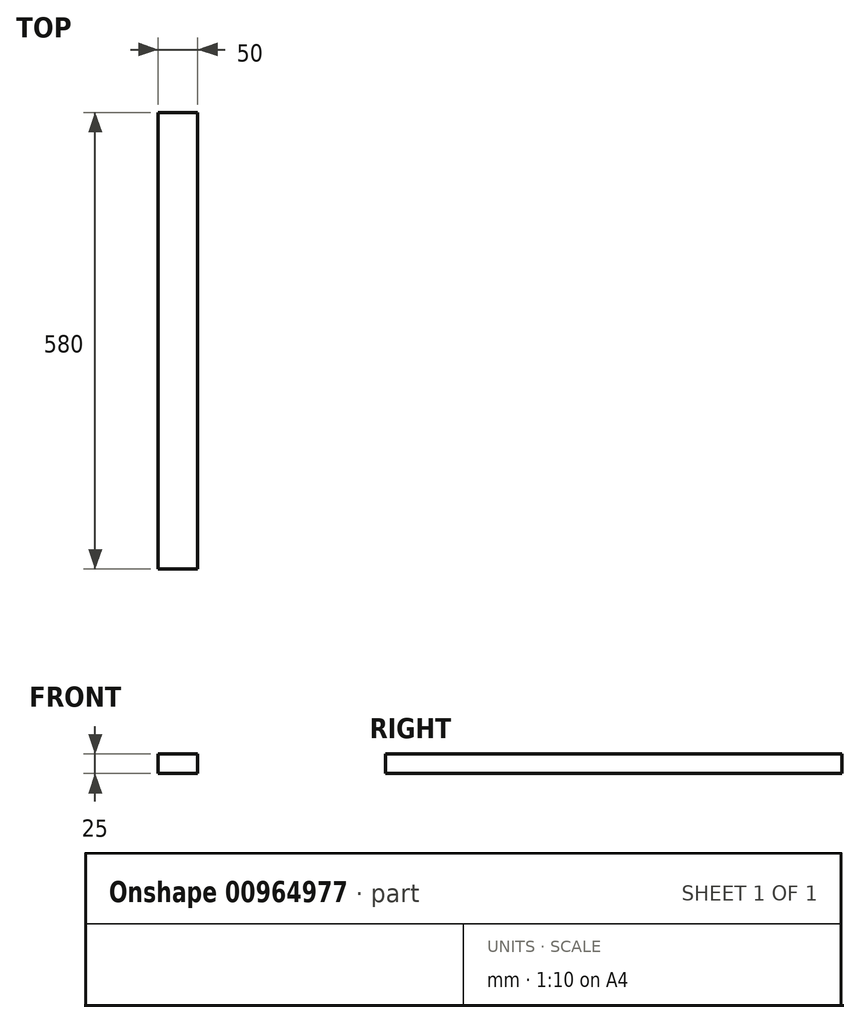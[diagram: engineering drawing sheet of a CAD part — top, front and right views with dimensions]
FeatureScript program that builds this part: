
annotation { "Feature Type Name" : "Feature", "Feature Type Description" : "" }
export const myFeature = defineFeature(function(context is Context, id is Id, definition is map)
    precondition{}
    {
        {
            var Q0;
            Q0=qCreatedBy(makeId("Top.planeOp"),FACE);
            var sketch = newSketch(context, id + "F0", { "sketchPlane" : qUnion([Q0])});
            skLineSegment(sketch, "E0.bottom", {"start": v(-2828.7, -249.1) * mm, "end": v(-2878.7, -249.1) * mm});
            skLineSegment(sketch, "E0.top", {"start": v(-2828.7, 330.9) * mm, "end": v(-2878.7, 330.9) * mm});
            skLineSegment(sketch, "E0.left", {"start": v(-2828.7, -249.1) * mm, "end": v(-2828.7, 330.9) * mm});
            skLineSegment(sketch, "E0.right", {"start": v(-2878.7, -249.1) * mm, "end": v(-2878.7, 330.9) * mm});
            skPoint(sketch, "E0.middle", {"position": v(-2853.7, 40.9) * mm});
            skSolve(sketch);
        }
        {
            var Q0;
            Q0=makeQuery(id+"F0.imprint","IMPRINT",FACE,{"disambiguationData":[TD([[makeQuery(id+"F0.imprint","IMPRINT",EDGE,{"derivedFrom":sQuery(id+"F0.wireOp",EDGE,"E0.bottom")}),-1.0]])]});
            extrude(context, id + "F1", {"entities" : qUnion([Q0]), "depth" : 25 * mm, "offsetDistance" : 25 * mm});
        }
    });
